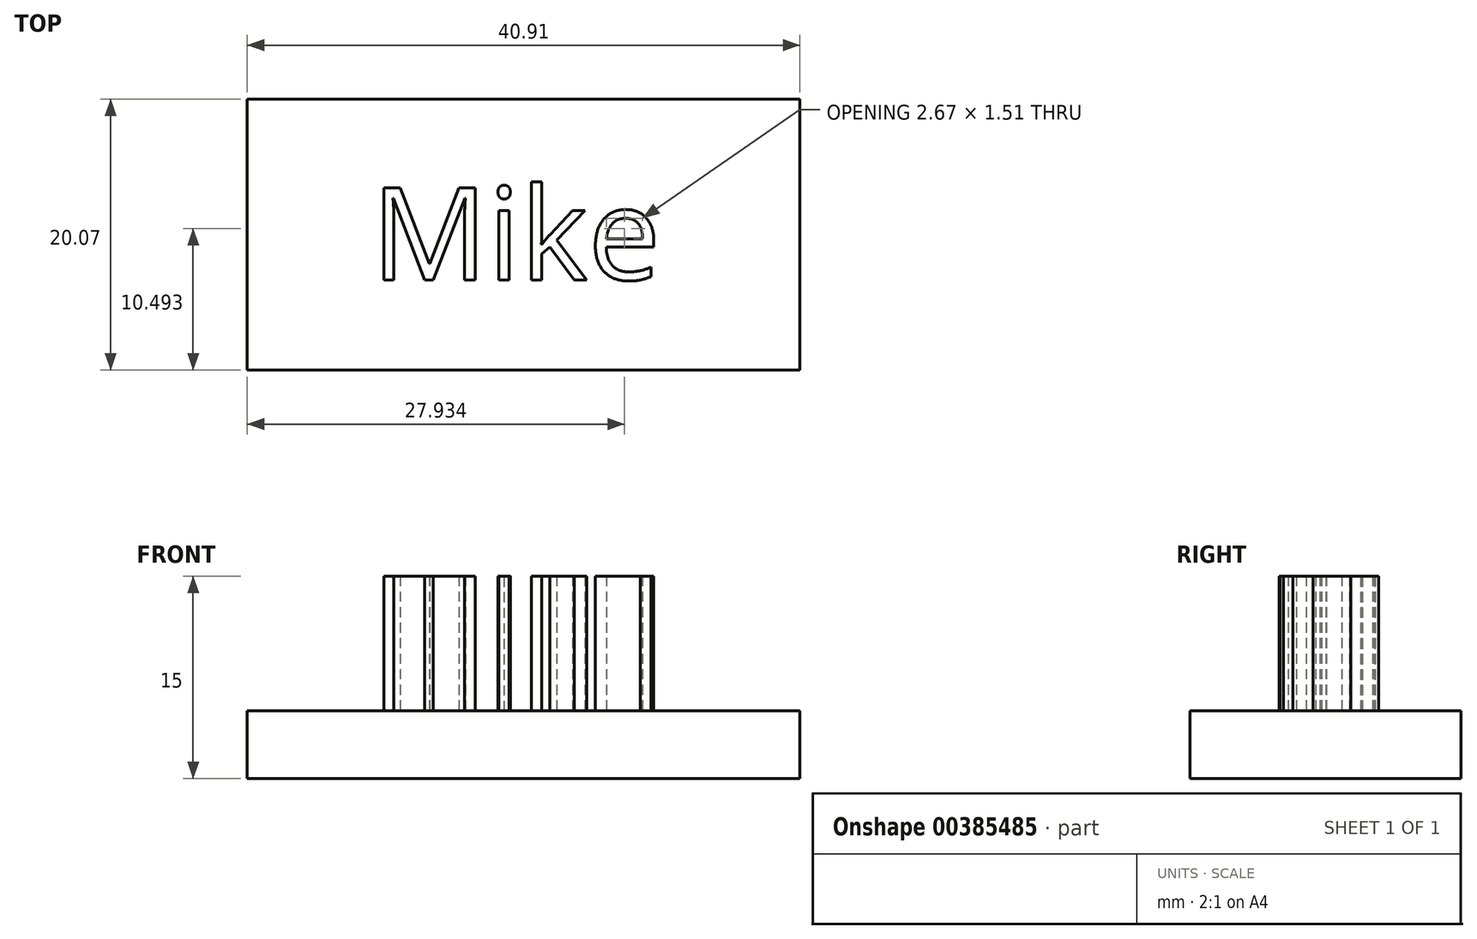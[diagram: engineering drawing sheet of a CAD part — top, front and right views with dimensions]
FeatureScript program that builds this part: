
annotation { "Feature Type Name" : "Feature", "Feature Type Description" : "" }
export const myFeature = defineFeature(function(context is Context, id is Id, definition is map)
    precondition{}
    {
        {
            var Q0;
            Q0=qCreatedBy(makeId("Top.planeOp"),FACE);
            var sketch = newSketch(context, id + "F0", { "sketchPlane" : qUnion([Q0])});
            skLineSegment(sketch, "E0.bottom", {"start": v(-72.84, 51.52) * mm, "end": v(-31.93, 51.52) * mm});
            skLineSegment(sketch, "E0.top", {"start": v(-72.84, 31.45) * mm, "end": v(-31.93, 31.45) * mm});
            skLineSegment(sketch, "E0.left", {"start": v(-72.84, 51.52) * mm, "end": v(-72.84, 31.45) * mm});
            skLineSegment(sketch, "E0.right", {"start": v(-31.93, 51.52) * mm, "end": v(-31.93, 31.45) * mm});
            skSolve(sketch);
        }
        {
            var Q0;
            Q0=makeQuery(id+"F0.imprint","IMPRINT",FACE,{"disambiguationData":[TD([[makeQuery(id+"F0.imprint","IMPRINT",EDGE,{"derivedFrom":sQuery(id+"F0.wireOp",EDGE,"E0.bottom")}),-1.0]])]});
            var sketch = newSketch(context, id + "F1", { "sketchPlane" : qUnion([Q0])});
            skText(sketch, "E1", { "text": "Mike", "fontName": "OpenSans-Regular.ttf"});
            const initialGuessF1  = {"E1": [-0.06366, 0.03814, 1, 0, 0.00688]};
            skSetInitialGuess(sketch, initialGuessF1);
            skSolve(sketch);
        }
        {
            var Q0;
            Q0 = qSketchRegion(id + "F1", true);
            extrude(context, id + "F2", {"entities" : qUnion([Q0]), "depth" : 10 * mm});
        }
        {
            var Q0;
            Q0=makeQuery(id+"F0.imprint","IMPRINT",FACE,{"disambiguationData":[TD([[makeQuery(id+"F0.imprint","IMPRINT",EDGE,{"derivedFrom":sQuery(id+"F0.wireOp",EDGE,"E0.bottom")}),-1.0]])]});
            extrude(context, id + "F3", {"entities" : qUnion([Q0]), "oppositeDirection" : true, "depth" : 5 * mm});
        }
    });
